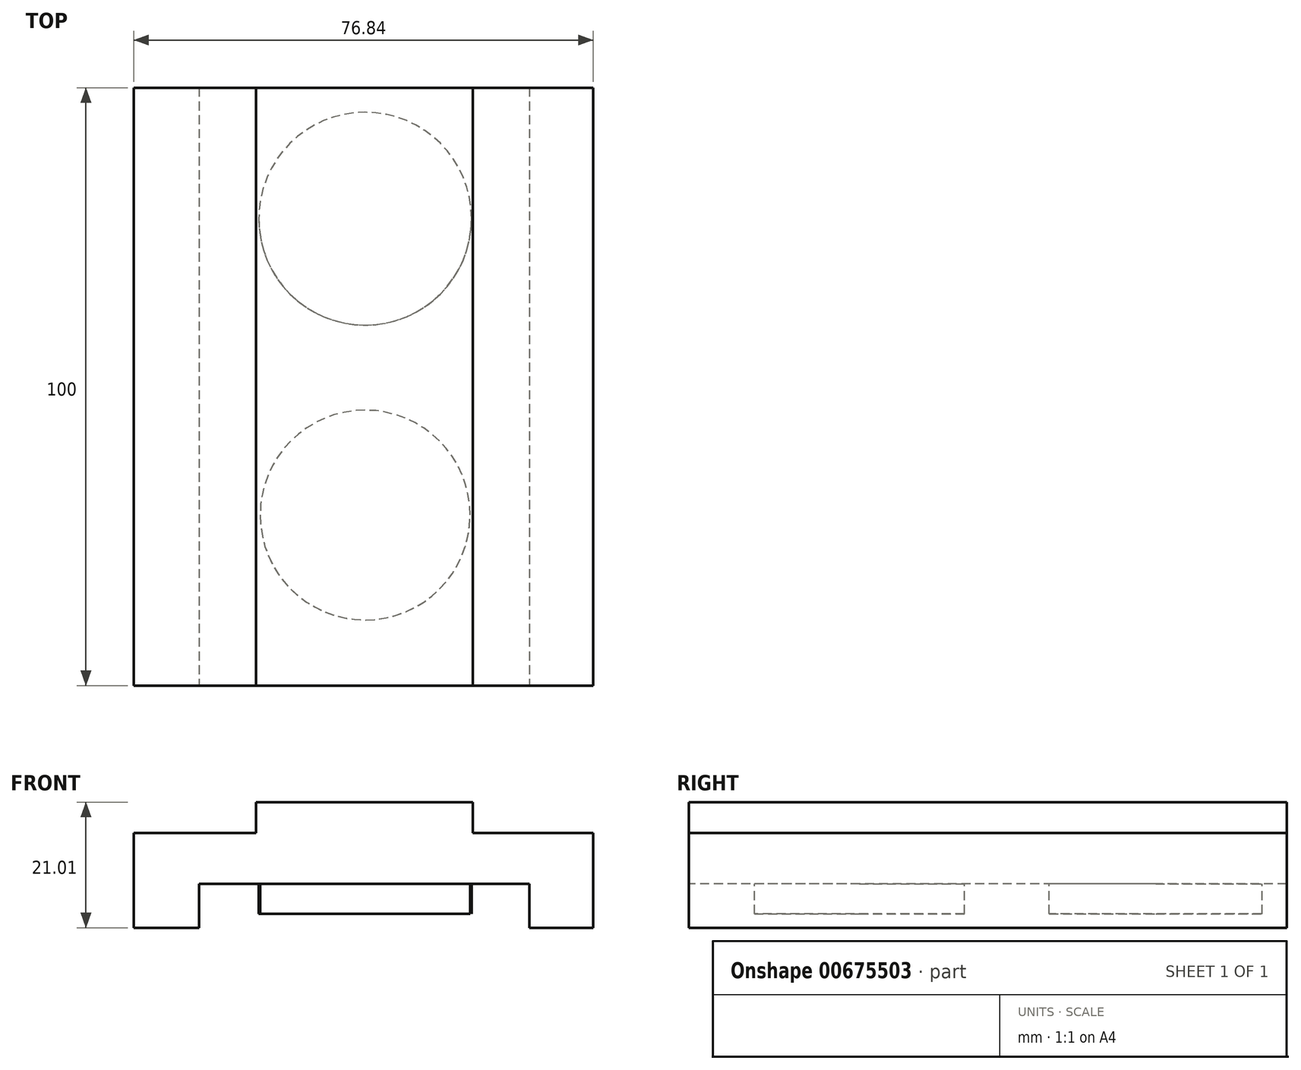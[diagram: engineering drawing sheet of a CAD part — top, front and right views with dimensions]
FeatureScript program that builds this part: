
annotation { "Feature Type Name" : "Feature", "Feature Type Description" : "" }
export const myFeature = defineFeature(function(context is Context, id is Id, definition is map)
    precondition{}
    {
        {
            var Q0;
            Q0=qCreatedBy(makeId("Front.planeOp"),FACE);
            var sketch = newSketch(context, id + "F0", { "sketchPlane" : qUnion([Q0])});
            skLineSegment(sketch, "E0.bottom", {"start": v(-27.77, 8.5) * mm, "end": v(-18.28, 8.5) * mm});
            skLineSegment(sketch, "E0.top", {"start": v(-27.77, 0) * mm, "end": v(27.49, 0) * mm});
            skLineSegment(sketch, "E1.bottom", {"start": v(27.49, 8.5) * mm, "end": v(38.13, 8.5) * mm});
            skLineSegment(sketch, "E1.top", {"start": v(27.49, -7.34) * mm, "end": v(38.13, -7.34) * mm});
            skLineSegment(sketch, "E1.left", {"start": v(27.49, 0) * mm, "end": v(27.49, -7.34) * mm});
            skLineSegment(sketch, "E1.right", {"start": v(38.13, 8.5) * mm, "end": v(38.13, -7.34) * mm});
            skLineSegment(sketch, "E2.bottom", {"start": v(-27.77, 8.5) * mm, "end": v(-38.7, 8.5) * mm});
            skLineSegment(sketch, "E2.top", {"start": v(-27.77, -7.34) * mm, "end": v(-38.7, -7.34) * mm});
            skLineSegment(sketch, "E2.right", {"start": v(-38.7, 8.5) * mm, "end": v(-38.7, -7.34) * mm});
            skLineSegment(sketch, "E3.top", {"start": v(-18.28, 13.67) * mm, "end": v(17.99, 13.67) * mm});
            skLineSegment(sketch, "E3.left", {"start": v(-18.28, 8.5) * mm, "end": v(-18.28, 13.67) * mm});
            skLineSegment(sketch, "E3.right", {"start": v(17.99, 8.5) * mm, "end": v(17.99, 13.67) * mm});
            skLineSegment(sketch, "E4.trimOffspring", {"start": v(17.99, 8.5) * mm, "end": v(27.49, 8.5) * mm});
            skLineSegment(sketch, "E5", {"start": v(-27.77, -7.34) * mm, "end": v(-27.77, 0) * mm});
            skSolve(sketch);
        }
        {
            var Q0;
            Q0=makeQuery(id+"F0.imprint","IMPRINT",FACE,{"disambiguationData":[TD([[makeQuery(id+"F0.imprint","IMPRINT",EDGE,{"derivedFrom":sQuery(id+"F0.wireOp",EDGE,"E0.bottom")}),-1.0]])]});
            extrude(context, id + "F1", {"entities" : qUnion([Q0]), "oppositeDirection" : true, "depth" : 100 * mm, "offsetDistance" : 25 * mm});
        }
        {
            var Q0;
            Q0=qCreatedBy(makeId("Top.planeOp"),FACE);
            var sketch = newSketch(context, id + "F2", { "sketchPlane" : qUnion([Q0])});
            skCircle(sketch, "E6", {"center": v(0, 28.53) * mm, "radius": 17.55 * mm});
            skCircle(sketch, "E7", {"center": v(0, 78.1) * mm, "radius": 17.8 * mm});
            skSolve(sketch);
        }
        {
            var Q0;
            Q0 = qSketchRegion(id + "F2", true);
            extrude(context, id + "F3", {"entities" : qUnion([Q0]), "operationType" : NewBodyOperationType.ADD, "oppositeDirection" : true, "depth" : 5 * mm, "offsetDistance" : 25 * mm});
        }
    });
